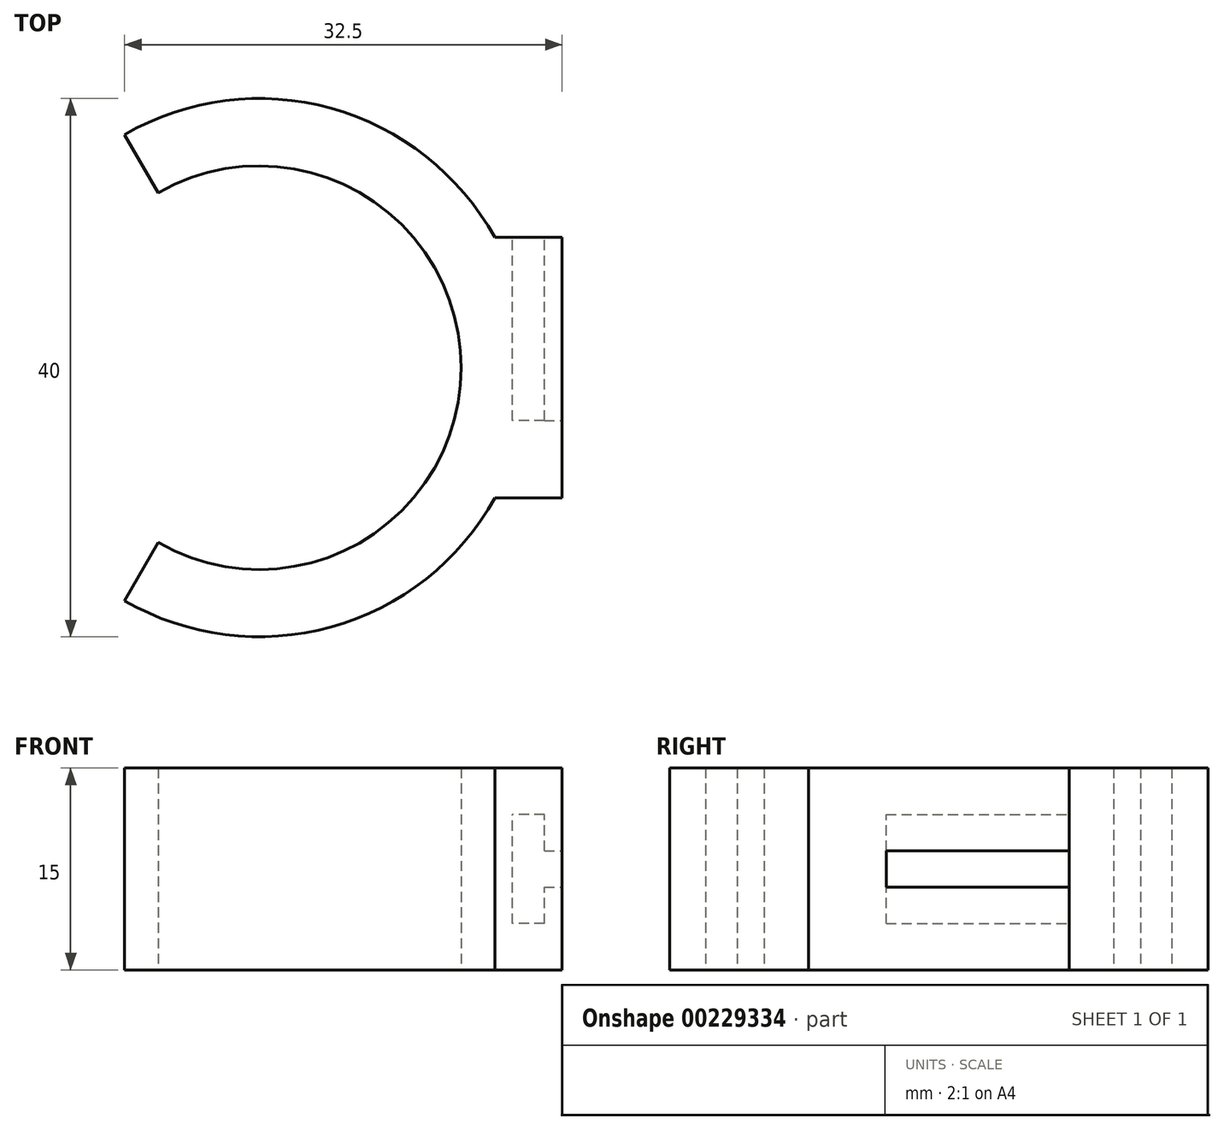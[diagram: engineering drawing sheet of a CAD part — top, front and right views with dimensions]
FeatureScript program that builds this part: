
annotation { "Feature Type Name" : "Feature", "Feature Type Description" : "" }
export const myFeature = defineFeature(function(context is Context, id is Id, definition is map)
    precondition{}
    {
        {
            var Q0;
            Q0=qCreatedBy(makeId("Top.planeOp"),FACE);
            var sketch = newSketch(context, id + "F0", { "sketchPlane" : qUnion([Q0])});
            skArc(sketch, "E0", {"start": v(-7.5, -13) * mm, "mid": v(15, 0) * mm, "end": v(-7.5, 13) * mm});
            skArc(sketch, "E1.0", {"start": v(-10, -17.32) * mm, "mid": v(5.35, -19.27) * mm, "end": v(17.5, -9.68) * mm});
            skLineSegment(sketch, "E2", {"start": v(-7.5, 13) * mm, "end": v(-10, 17.32) * mm});
            skLineSegment(sketch, "E3", {"start": v(-7.5, -13) * mm, "end": v(-10, -17.32) * mm});
            skLineSegment(sketch, "E4.bottom", {"start": v(22.5, -9.68) * mm, "end": v(17.5, -9.68) * mm});
            skLineSegment(sketch, "E4.top", {"start": v(22.5, 9.68) * mm, "end": v(17.5, 9.68) * mm});
            skLineSegment(sketch, "E4.left", {"start": v(22.5, -9.68) * mm, "end": v(22.5, 9.68) * mm});
            skPoint(sketch, "E4.middle", {"position": v(20, 0) * mm});
            skArc(sketch, "E5.trimOffspring", {"start": v(17.5, 9.68) * mm, "mid": v(5.35, 19.27) * mm, "end": v(-10, 17.32) * mm});
            skSolve(sketch);
        }
        {
            var Q0;
            Q0=makeQuery(id+"F0.imprint","IMPRINT",FACE,{"disambiguationData":[TD([[makeQuery(id+"F0.imprint","IMPRINT",EDGE,{"derivedFrom":sQuery(id+"F0.wireOp",EDGE,"E0")}),-1.0]])]});
            extrude(context, id + "F1", {"entities" : qUnion([Q0]), "depth" : 15 * mm});
        }
        {
            var Q0;
            Q0=makeQuery(id+"F1.opExtrude","SWEPT_FACE",FACE,{"disambiguationData":[OSD([sQuery(id+"F0.wireOp",EDGE,"E4.top")])]});
            var sketch = newSketch(context, id + "F2", { "sketchPlane" : qUnion([Q0])});
            skLineSegment(sketch, "E6.bottom", {"start": v(-21.19, 6.15) * mm, "end": v(-23.88, 6.15) * mm});
            skLineSegment(sketch, "E6.top", {"start": v(-21.19, 8.85) * mm, "end": v(-23.88, 8.85) * mm});
            skLineSegment(sketch, "E6.right", {"start": v(-23.88, 6.15) * mm, "end": v(-23.88, 8.85) * mm});
            skPoint(sketch, "E6.middle", {"position": v(-22.5, 7.5) * mm});
            skLineSegment(sketch, "E7", {"start": v(-22.5, 7.5) * mm, "end": v(-18.06, 7.5) * mm, "construction": true});
            skLineSegment(sketch, "E8", {"start": v(-20, 15) * mm, "end": v(-20, 0) * mm, "construction": true});
            skLineSegment(sketch, "E9.bottom", {"start": v(-21.19, 3.44) * mm, "end": v(-18.81, 3.44) * mm});
            skLineSegment(sketch, "E9.top", {"start": v(-21.19, 11.56) * mm, "end": v(-18.81, 11.56) * mm});
            skLineSegment(sketch, "E9.left", {"start": v(-21.19, 3.44) * mm, "end": v(-21.19, 6.15) * mm});
            skLineSegment(sketch, "E9.right", {"start": v(-18.81, 3.44) * mm, "end": v(-18.81, 11.56) * mm});
            skPoint(sketch, "E9.middle", {"position": v(-20, 7.5) * mm});
            skLineSegment(sketch, "E10.trimOffspring", {"start": v(-21.19, 8.85) * mm, "end": v(-21.19, 11.56) * mm});
            skPoint(sketch, "E11.orphan", {"position": v(-21.12, 8.85) * mm});
            skPoint(sketch, "E12.orphan", {"position": v(-21.12, 6.15) * mm});
            skSolve(sketch);
        }
        {
            var Q0;
            Q0=makeQuery(id+"F2.imprint","IMPRINT",FACE,{"disambiguationData":[TD([[makeQuery(id+"F2.imprint","IMPRINT",EDGE,{"derivedFrom":sQuery(id+"F2.wireOp",EDGE,"E9.bottom")}),1.0]])]});
            var Q1;
            {var subQ0=sQuery(id+"F2.wireOp",EDGE,"E6.right");Q1=makeQuery(id+"F2.imprint","IMPRINT",FACE,{"disambiguationData":[TD([[makeQuery(id+"F2.imprint","IMPRINT",EDGE,{"derivedFrom":subQ0}),-1.0]])]});}
            extrude(context, id + "F3", {"entities" : qUnion([Q0, Q1]), "operationType" : NewBodyOperationType.REMOVE, "oppositeDirection" : true, "depth" : 13.6 * mm});
        }
    });
